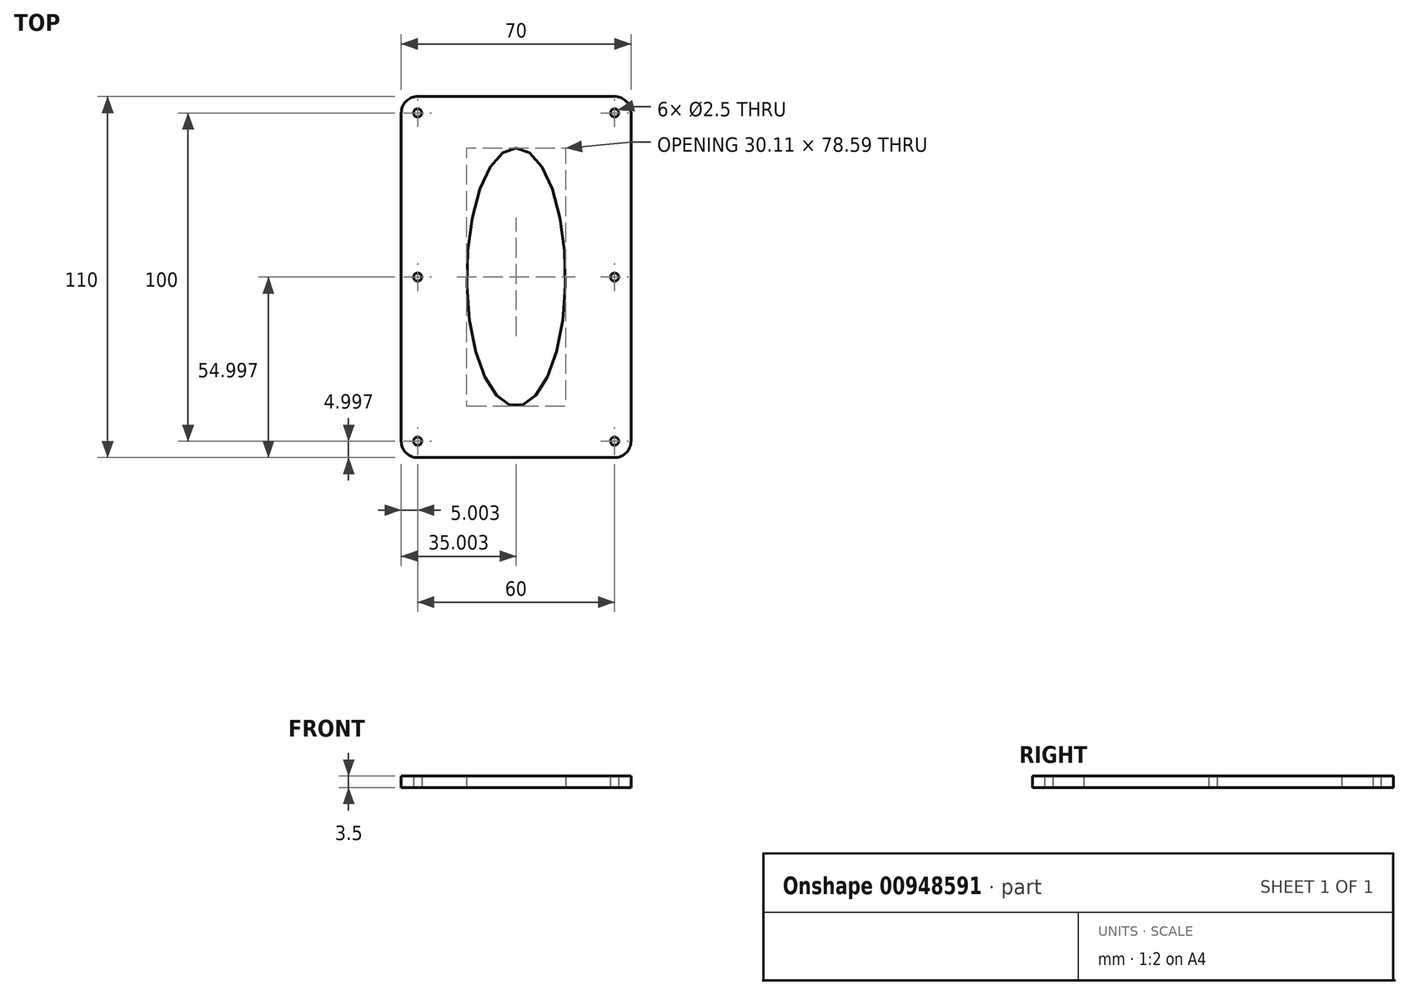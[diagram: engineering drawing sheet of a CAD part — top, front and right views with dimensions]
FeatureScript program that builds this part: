
annotation { "Feature Type Name" : "Feature", "Feature Type Description" : "" }
export const myFeature = defineFeature(function(context is Context, id is Id, definition is map)
    precondition{}
    {
        {
            var Q0;
            Q0=qCreatedBy(makeId("Top.planeOp"),FACE);
            var sketch = newSketch(context, id + "F0", { "sketchPlane" : qUnion([Q0])});
            skLineSegment(sketch, "E0.bottom", {"start": v(-2.06, 93.87) * mm, "end": v(-62.06, 93.87) * mm});
            skLineSegment(sketch, "E0.top", {"start": v(-2.06, -16.13) * mm, "end": v(-62.06, -16.13) * mm});
            skLineSegment(sketch, "E0.left", {"start": v(2.94, 88.87) * mm, "end": v(2.94, -11.13) * mm});
            skLineSegment(sketch, "E0.right", {"start": v(-67.06, 88.87) * mm, "end": v(-67.06, -11.13) * mm});
            skPoint(sketch, "E0.middle", {"position": v(-32.06, 38.87) * mm});
            skLineSegment(sketch, "E1.bottom", {"start": v(-7.06, 80.67) * mm, "end": v(-57.06, 80.67) * mm});
            skLineSegment(sketch, "E1.top", {"start": v(-7.06, -2.93) * mm, "end": v(-57.06, -2.93) * mm});
            skLineSegment(sketch, "E1.left", {"start": v(-7.06, 80.67) * mm, "end": v(-7.06, -2.93) * mm});
            skLineSegment(sketch, "E1.right", {"start": v(-57.06, 80.67) * mm, "end": v(-57.06, -2.93) * mm});
            skLineSegment(sketch, "E2.top", {"start": v(-59.1, 93.87) * mm, "end": v(-5, 93.87) * mm});
            skLineSegment(sketch, "E2.left", {"start": v(-59.1, 81.67) * mm, "end": v(-59.1, 93.87) * mm});
            skLineSegment(sketch, "E2.right", {"start": v(-5, 81.67) * mm, "end": v(-5, 93.87) * mm});
            skPoint(sketch, "E3.visualSharp", {"position": v(-67.06, 93.87) * mm});
            skArc(sketch, "E3.filletArc", {"start": v(-62.06, 93.87) * mm, "mid": v(-65.6, 92.4) * mm, "end": v(-67.06, 88.87) * mm});
            skPoint(sketch, "E4.visualSharp", {"position": v(2.94, 93.87) * mm});
            skArc(sketch, "E4.filletArc", {"start": v(2.94, 88.87) * mm, "mid": v(1.48, 92.4) * mm, "end": v(-2.06, 93.87) * mm});
            skPoint(sketch, "E5.visualSharp", {"position": v(2.94, -16.13) * mm});
            skArc(sketch, "E5.filletArc", {"start": v(-2.06, -16.13) * mm, "mid": v(1.48, -14.67) * mm, "end": v(2.94, -11.13) * mm});
            skPoint(sketch, "E6.visualSharp", {"position": v(-67.06, -16.13) * mm});
            skArc(sketch, "E6.filletArc", {"start": v(-67.06, -11.13) * mm, "mid": v(-65.6, -14.67) * mm, "end": v(-62.06, -16.13) * mm});
            skCircle(sketch, "E7", {"center": v(-62.06, 88.87) * mm, "radius": 1.25 * mm});
            skCircle(sketch, "E8", {"center": v(-2.06, 88.87) * mm, "radius": 1.25 * mm});
            skCircle(sketch, "E9", {"center": v(-62.06, -11.13) * mm, "radius": 1.25 * mm});
            skCircle(sketch, "E10", {"center": v(-2.06, -11.13) * mm, "radius": 1.25 * mm});
            skCircle(sketch, "E11", {"center": v(-62.06, 38.87) * mm, "radius": 1.25 * mm});
            skCircle(sketch, "E12", {"center": v(-2.06, 38.87) * mm, "radius": 1.25 * mm});
            skLineSegment(sketch, "E13.top", {"start": v(-59.1, -3.93) * mm, "end": v(-5, -3.93) * mm});
            skLineSegment(sketch, "E13.left", {"start": v(-59.1, 93.87) * mm, "end": v(-59.1, -3.93) * mm});
            skLineSegment(sketch, "E13.right", {"start": v(-5, 93.87) * mm, "end": v(-5, -3.93) * mm});
            skCircle(sketch, "E14", {"center": v(-56.9, -1.58) * mm, "radius": 3.25 * mm});
            skCircle(sketch, "E15", {"center": v(-7.11, -1.68) * mm, "radius": 3.25 * mm});
            skEllipse(sketch, "E16", {"center": v(-32.06, 38.87) * mm, "majorRadius": 39.3 * mm, "minorRadius": 15.06 * mm, "majorAxis": v(0, 1)});
            skSolve(sketch);
        }
        {
            var Q0;
            Q0=makeQuery(id+"F0.imprint","IMPRINT",FACE,{"disambiguationData":[TD([[makeQuery(id+"F0.imprint","IMPRINT",EDGE,{"derivedFrom":sQuery(id+"F0.wireOp",EDGE,"E0.top")}),-1.0]])]});
            var Q1;
            {var subQ2=sQuery(id+"F0.wireOp",EDGE,"E1.bottom");Q1=makeQuery(id+"F0.imprint","IMPRINT",FACE,{"disambiguationData":[TD([[makeQuery(id+"F0.imprint","IMPRINT",EDGE,{"derivedFrom":subQ2}),-1.0]])]});}
            var Q2;
            {var subQ1=sQuery(id+"F0.wireOp",EDGE,"E1.bottom");Q2=makeQuery(id+"F0.imprint","IMPRINT",FACE,{"disambiguationData":[TD([[makeQuery(id+"F0.imprint","IMPRINT",EDGE,{"derivedFrom":subQ1}),1.0]])]});}
            var Q3;
            {var subQ6=sQuery(id+"F0.wireOp",EDGE,"E1.top");var subQ8=sQuery(id+"F0.wireOp",EDGE,"E1.right");var subQ9=makeQuery(id+"F0.imprint","INTERSECT",VERTEX,{"derivedFrom":[subQ6,subQ8]});Q3=makeQuery(id+"F0.imprint","IMPRINT",FACE,{"disambiguationData":[TD([[makeQuery(id+"F0.imprint","IMPRINT",EDGE,{"disambiguationData":[TD([[subQ9,1.0]])],"derivedFrom":subQ6}),1.0]])]});}
            var Q4;
            {var subQ0=sQuery(id+"F0.wireOp",EDGE,"E1.right");var subQ1=sQuery(id+"F0.wireOp",EDGE,"E1.top");var subQ2=makeQuery(id+"F0.imprint","INTERSECT",VERTEX,{"derivedFrom":[subQ1,subQ0]});Q4=makeQuery(id+"F0.imprint","IMPRINT",FACE,{"disambiguationData":[TD([[makeQuery(id+"F0.imprint","IMPRINT",EDGE,{"disambiguationData":[TD([[subQ2,1.0]])],"derivedFrom":subQ1}),-1.0]])]});}
            var Q5;
            {var subQ0=sQuery(id+"F0.wireOp",EDGE,"E13.left");var subQ1=sQuery(id+"F0.wireOp",EDGE,"E13.top");var subQ2=makeQuery(id+"F0.imprint","INTERSECT",VERTEX,{"derivedFrom":[subQ1,subQ0]});Q5=makeQuery(id+"F0.imprint","IMPRINT",FACE,{"disambiguationData":[TD([[makeQuery(id+"F0.imprint","IMPRINT",EDGE,{"disambiguationData":[TD([[subQ2,-1.0]])],"derivedFrom":subQ1}),-1.0]])]});}
            var Q6;
            {var subQ0=sQuery(id+"F0.wireOp",EDGE,"E15");var subQ1=sQuery(id+"F0.wireOp",EDGE,"E1.top");var subQ2=makeQuery(id+"F0.imprint","INTERSECT",VERTEX,{"derivedFrom":[subQ1,subQ0]});Q6=makeQuery(id+"F0.imprint","IMPRINT",FACE,{"disambiguationData":[TD([[makeQuery(id+"F0.imprint","IMPRINT",EDGE,{"disambiguationData":[TD([[subQ2,-1.0]])],"derivedFrom":subQ1}),1.0]])]});}
            var Q7;
            {var subQ0=sQuery(id+"F0.wireOp",EDGE,"E13.right");var subQ1=sQuery(id+"F0.wireOp",EDGE,"E13.top");var subQ2=makeQuery(id+"F0.imprint","INTERSECT",VERTEX,{"derivedFrom":[subQ1,subQ0]});Q7=makeQuery(id+"F0.imprint","IMPRINT",FACE,{"disambiguationData":[TD([[makeQuery(id+"F0.imprint","IMPRINT",EDGE,{"disambiguationData":[TD([[subQ2,1.0]])],"derivedFrom":subQ1}),-1.0]])]});}
            var Q8;
            {var subQ5=sQuery(id+"F0.wireOp",EDGE,"E1.left");var subQ6=sQuery(id+"F0.wireOp",EDGE,"E1.top");var subQ7=makeQuery(id+"F0.imprint","INTERSECT",VERTEX,{"derivedFrom":[subQ6,subQ5]});Q8=makeQuery(id+"F0.imprint","IMPRINT",FACE,{"disambiguationData":[TD([[makeQuery(id+"F0.imprint","IMPRINT",EDGE,{"disambiguationData":[TD([[subQ7,-1.0]])],"derivedFrom":subQ6}),1.0]])]});}
            var Q9;
            {var subQ0=sQuery(id+"F0.wireOp",EDGE,"E1.left");var subQ1=sQuery(id+"F0.wireOp",EDGE,"E1.top");var subQ2=makeQuery(id+"F0.imprint","INTERSECT",VERTEX,{"derivedFrom":[subQ1,subQ0]});Q9=makeQuery(id+"F0.imprint","IMPRINT",FACE,{"disambiguationData":[TD([[makeQuery(id+"F0.imprint","IMPRINT",EDGE,{"disambiguationData":[TD([[subQ2,-1.0]])],"derivedFrom":subQ1}),-1.0]])]});}
            extrude(context, id + "F1", {"entities" : qUnion([Q0, Q1, Q2, Q3, Q4, Q5, Q6, Q7, Q8, Q9]), "depth" : 3.5 * mm, "offsetDistance" : 25 * mm});
        }
    });
